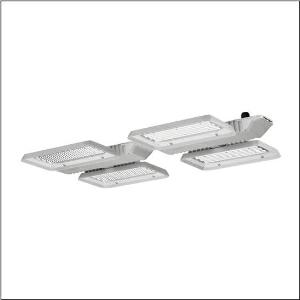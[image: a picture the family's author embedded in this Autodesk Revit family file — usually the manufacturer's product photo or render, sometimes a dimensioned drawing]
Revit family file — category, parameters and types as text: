
# Revit family: highbay_11_51hlasd24mga
name_source: partatom
category: Lighting Fixtures
units: mm (PartAtom-declared; Revit-internal decimal feet)

## family parameters
Cut with Voids When Loaded = No
Host = Face
Light Source = No
Part Type = Normal
Room Calculation Point = No
Round Connector Dimension = Use Diameter
Shared = No

## types (1)
- --- (1 x LED, 28800 lm, 162.6 W, 4000K)
    Apparent Load = 163 VA
    CIE Flux Codes = 89 96 99 100 100
    Color Rendering = 80
    Color Temperature = 4000K
    Default Elevation = 1800 mm
    Description = Highbay 11, LED high bay luminaire, primary light control with lens, of PMMA, light emission: direct distribution, primary light characteristic: symmetric, installation type: suspended mounting, for 2x 2x LED, rated luminous flux: 28.800lm, luminous efficacy: 177lm/W, light colour: 840, colour temperature: 4000K, control gear: ECG DALI, with terminal, 5-pole, max. 2.5mm², mains connection: 230..240V, AC, 50/60Hz, rated input power: 163W, LED unit, of diecast aluminium, unplated, bead blasted, silver, length: 940mm, width: 500mm, height: 65mm, housing, of diecast aluminium, uncoated, bead blasted, silver, protection rating (complete): IP20, insulation class (complete): insulation class I (protective earthing), certification: CE, ENEC, VDE, UKCA, protection symbol: D, ball protection: ball impact resistant according to DIN VDE 0710 part 13 (with chain suspension), permissible operating ambient temperature: -35..+55°C, corresponds to IFS (International Featured Standards) requirements for safety and quality in the food industry, reducing of maximum allowable ambient temperature of 5°C with ceiling mounting, packaging unit: 1 piece
    Height = 95 mm
    Lamp = 1 x LED
    Lamp Light Flux = 28800 lm
    Lamp Power = 162.6 W
    Lamp count = 1
    Length = 939 mm
    Luminous efficacy = 177 lm/W
    Manufacturer = Siteco
    ModVariant = No
    Model = 51HLASD24MGA
    Mounting Place = Ceiling
    Mounting Type = Pendant
    Number of Poles = 1
    OnlyDefault = Yes
    Power Factor = 1
    Product Name = Highbay 11
    Product group = LED high bay luminaire
    ProductGroupID = 903
    Protection Class = Protection class I
    Protection Degree = IP 20
    RLX_Detail_Level = 1
    RLX_Emergency_Light_Flux = 0 lm
    RLX_Emergency_Type = 0
    RLX_Emergency_Type_DB = No
    RlxData = <blob elided: 64373 chars, md5=006fd293>
    Socket = socket
    Standby Power = 0 W
    System Light Flux = 28800 lm
    System Power = 163 W
    Type Comments = factory setting: luminous flux: 100 % | dim-lin: 254 | 460 mA
    Type Image = l_1006021.jpg
    URL = http://relux.com
    VarID = @adj_158243
    Voltage = 0 V
    Weight = 0.00 kg
    Width = 501 mm

## geometry (parser evidence)
native form markers: Blend x4, Sweep x12
no freeform markers — native parametric forms only
